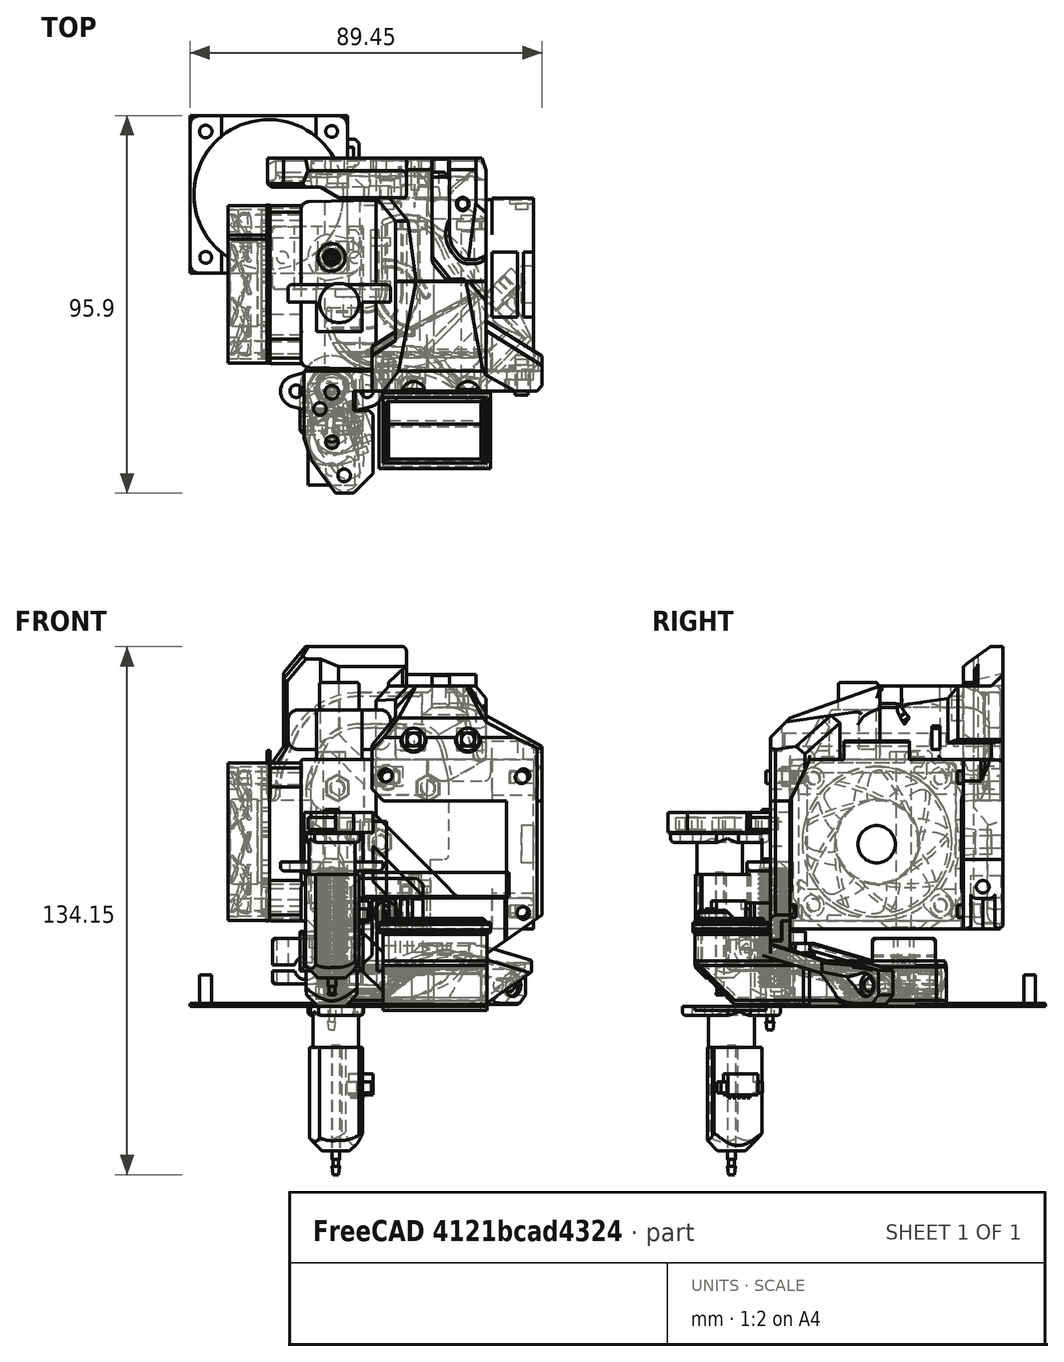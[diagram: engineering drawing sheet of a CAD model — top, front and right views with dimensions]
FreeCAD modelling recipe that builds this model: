
FCSTD DOCUMENT  (FreeCAD 0.18R16146 (Git))
Label: bearmera-4020-rev-1
License: All rights reserved
LicenseURL: http://en.wikipedia.org/wiki/All_rights_reserved
objects: Part::Box×71, Part::Cut×55, Part::Feature×46, Part::MultiFuse×39, Part::Chamfer×34, Part::Cylinder×33, Sketcher::SketchObject×6, PartDesign::Body×4, App::DocumentObjectGroup×3, Part::MultiCommon×3, Mesh::Feature×2, PartDesign::AdditiveLoft×2, PartDesign::Pad×2, App::Part×1
note: 299 computed .brp shape members not serialized (recipe doc carries the construction recipe); baked Part::Feature solids carry a one-line shape summary decoded from their .brp

FEATURE [Part::Feature] Part__Feature018  label="NOZZLE-POS"
  Placement = pos=(-0.025,3.1e-14,12.45) rot=(0.707107,0.707107,0;3.14159rad)
  shape: bbox 8.083 x 7 x 12.5 mm, 18 faces (baked)
FEATURE [Part::Feature] Part__Feature017  label="v6_heaterblock v1"
  Placement = pos=(-14.9885,-8.00025,5.758) rot=(0,0,1;0rad)
  shape: bbox 23 x 16 x 11.5 mm, 37 faces (baked)
FEATURE [Part::Feature] Part__Feature013  label="stepper"
  Placement = pos=(51.225,-28.9,19.7) rot=(0,0,1;1.5708rad)
  shape: bbox 40 x 44 x 47.7 mm, 101 faces (baked)
FEATURE [Part::Feature] Part__Feature014  label="heatsink"
  Placement = pos=(11.225,-28.4,19.7) rot=(0,0,1;1.5708rad)
  shape: bbox 30.92 x 43.26 x 62.61 mm, 110 faces (baked)
FEATURE [Part::Feature] Part__Feature016  label="e3d_hemera_fan v1"
  Placement = pos=(-15.775,13.2,61.8) rot=(0.57735,-0.57735,0.57735;4.18879rad)
  shape: bbox 10.51 x 40.01 x 40.01 mm, 129 faces (baked)
FEATURE [Mesh::Feature] lower_4020_fan_duct  label="lower_4020-fan-duct"
  Placement = pos=(11.3,-33.9,19.8) rot=(0,0,1;0rad)
FEATURE [Part::Feature] Cut007002001001  label="fan-mount-frame001"
  shape: bbox 28.2 x 19.2 x 3.5 mm, 16 faces (baked)
FEATURE [Part::Feature] Part__Feature  label="duct001"
  Placement = pos=(13,-15,0) rot=(0,0,1;0rad)
  shape: bbox 62.87 x 53.67 x 16.75 mm, 145 faces (baked)
FEATURE [Part::Feature] Part__Feature025  label="duct002"
  Placement = pos=(13,-15,0) rot=(0,0,1;0rad)
  shape: bbox 62.87 x 53.67 x 16.75 mm, 145 faces (baked)
FEATURE [Part::Box] Box  label="Cube"
  AttacherType = Attacher::AttachEngine3D
  Height = 17
  Length = 29
  Placement = pos=(26,-38,0) rot=(0,0,1;0rad)
  Width = 48
FEATURE [Part::Box] Box001  label="Cube001"
  AttacherType = Attacher::AttachEngine3D
  Height = 27
  Length = 26
  Placement = pos=(0,-34,0) rot=(0,0,1;0rad)
  Width = 10
FEATURE [Part::Cut] Cut
  Base = -> Part__Feature
  Tool = -> Box
FEATURE [Part::Cut] Cut007002001002
  Base = -> Cut
  Placement = pos=(0,0,-0.45) rot=(0,0,1;0rad)
  Tool = -> Box001
FEATURE [Part::Box] Box002  label="Cube002"
  AttacherType = Attacher::AttachEngine3D
  Height = 2
  Length = 13
  Placement = pos=(13,-24,0.8) rot=(0,0,1;0rad)
  Width = 4
FEATURE [Part::Box] Box003  label="Cube003"
  AttacherType = Attacher::AttachEngine3D
  Height = 1
  Length = 5
  Placement = pos=(21,-24,0.8) rot=(0,0,1;0rad)
  Width = 13
FEATURE [Part::Cut] Cut007002001003
  Base = -> Cut007002001002
  Tool = -> Box002
FEATURE [Part::Cut] Cut007002001004
  Base = -> Cut007002001003
  Tool = -> Box003
FEATURE [Part::Box] Box004  label="Cube004"
  AttacherType = Attacher::AttachEngine3D
  Height = 10
  Length = 24
  Placement = pos=(7,-30,10) rot=(0,0,1;0rad)
  Width = 27
FEATURE [Part::Cut] Cut007002001005
  Base = -> Cut007002001004
  Tool = -> Box004
FEATURE [Part::Box] Box005  label="Cube005"
  AttacherType = Attacher::AttachEngine3D
  Height = 10
  Length = 32
  Placement = pos=(-2,-38,0) rot=(0,0,1;0rad)
  Width = 14
FEATURE [Part::Box] Box007  label="Cube007"
  AttacherType = Attacher::AttachEngine3D
  Height = 10
  Length = 21
  Placement = pos=(26,-24,0) rot=(0,0,1;0rad)
  Width = 21
FEATURE [Part::Box] Box008  label="Cube008"
  AttacherType = Attacher::AttachEngine3D
  Height = 1
  Length = 41
  Placement = pos=(10,-35,9) rot=(0,0,1;0.506145rad)
  Width = 10
FEATURE [Part::MultiFuse] Fusion
  Shapes = -> [Cut007002001005,Box008]
FEATURE [Part::Cut] Cut007002001006
  Base = -> Fusion
  Tool = -> Box005
FEATURE [Part::Cut] Cut007002001007  label="duct-square-cut"
  Base = -> Cut007002001006
  Tool = -> Box007
FEATURE [Part::Feature] Cut007002001007001  label="Cut007002001008"
  shape: bbox 41.3 x 51.61 x 10 mm, 88 faces (baked)
FEATURE [Part::Box] Box012  label="Cube012"
  AttacherType = Attacher::AttachEngine3D
  Height = 1
  Length = 26.5
  Placement = pos=(13,-53,0) rot=(0,0,1;0rad)
  Width = 18
FEATURE [Part::Box] Box013  label="Cube013"
  AttacherType = Attacher::AttachEngine3D
  Height = 1
  Length = 23.5
  Placement = pos=(14.5,-51.5,0) rot=(0,0,1;0rad)
  Width = 15
FEATURE [Part::Cut] Cut007002001007002
  Base = -> Box012
  Placement = pos=(0,0,-1) rot=(0,0,1;0rad)
  Tool = -> Box013
FEATURE [Sketcher::SketchObject] Sketch
  AttachmentOffset = pos=(0,0,19) rot=(0,0,1;0rad)
  MapMode = 5
  Placement = pos=(0,0,19) rot=(0,0,1;0rad)
  Support = -> [XY_Plane]
  sketch-geometry (8):
    g0: LineSegment StartX=13 StartY=-35 StartZ=0 EndX=39.5 EndY=-35 EndZ=0
    g1: LineSegment StartX=39.5 StartY=-35 StartZ=0 EndX=39.5 EndY=-53 EndZ=0
    g2: LineSegment StartX=39.5 StartY=-53 StartZ=0 EndX=13 EndY=-53 EndZ=0
    g3: LineSegment StartX=13 StartY=-53 StartZ=0 EndX=13 EndY=-35 EndZ=0
    g4: LineSegment StartX=14.5 StartY=-36.5 StartZ=0 EndX=38 EndY=-36.5 EndZ=0
    g5: LineSegment StartX=38 StartY=-36.5 StartZ=0 EndX=38 EndY=-51.5 EndZ=0
    g6: LineSegment StartX=38 StartY=-51.5 StartZ=0 EndX=14.5 EndY=-51.5 EndZ=0
    g7: LineSegment StartX=14.5 StartY=-51.5 StartZ=0 EndX=14.5 EndY=-36.5 EndZ=0
  constraints (16):
    c: Coincident(g0,g1)
    c: Coincident(g1,g2)
    c: Coincident(g2,g3)
    c: Coincident(g3,g0)
    c: Horizontal(g0)
    c: Horizontal(g2)
    c: Vertical(g1)
    c: Vertical(g3)
    c: Coincident(g4,g5)
    c: Coincident(g5,g6)
    c: Coincident(g6,g7)
    c: Coincident(g7,g4)
    c: Horizontal(g4)
    c: Horizontal(g6)
    c: Vertical(g5)
    c: Vertical(g7)
FEATURE [Sketcher::SketchObject] Sketch001
  AttachmentOffset = pos=(0,0,10.45) rot=(0,0,1;0rad)
  MapMode = 5
  Placement = pos=(0,0,10.45) rot=(0,0,1;0rad)
  Support = -> [XY_Plane]
  sketch-geometry (8):
    g0: LineSegment StartX=13 StartY=-53 StartZ=0 EndX=39.5 EndY=-53 EndZ=0
    g1: LineSegment StartX=39.5 StartY=-53 StartZ=0 EndX=39.5 EndY=-24 EndZ=0
    g2: LineSegment StartX=39.5 StartY=-24 StartZ=0 EndX=13 EndY=-24 EndZ=0
    g3: LineSegment StartX=13 StartY=-24 StartZ=0 EndX=13 EndY=-53 EndZ=0
    g4: LineSegment StartX=38 StartY=-25.5 StartZ=0 EndX=14.5 EndY=-25.5 EndZ=0
    g5: LineSegment StartX=14.5 StartY=-25.5 StartZ=0 EndX=14.5 EndY=-51.5 EndZ=0
    g6: LineSegment StartX=14.5 StartY=-51.5 StartZ=0 EndX=38 EndY=-51.5 EndZ=0
    g7: LineSegment StartX=38 StartY=-51.5 StartZ=0 EndX=38 EndY=-25.5 EndZ=0
  constraints (16):
    c: Coincident(g0,g1)
    c: Coincident(g1,g2)
    c: Coincident(g2,g3)
    c: Coincident(g3,g0)
    c: Horizontal(g0)
    c: Horizontal(g2)
    c: Vertical(g1)
    c: Vertical(g3)
    c: Coincident(g4,g5)
    c: Coincident(g5,g6)
    c: Coincident(g6,g7)
    c: Coincident(g7,g4)
    c: Horizontal(g4)
    c: Horizontal(g6)
    c: Vertical(g5)
    c: Vertical(g7)
FEATURE [PartDesign::AdditiveLoft] AdditiveLoft
  Closed = false
  Profile = -> Sketch
  Ruled = false
  Sections = -> [Sketch001]
FEATURE [PartDesign::Body] Body  label="ramp"
  Group = -> [Sketch,Sketch001,AdditiveLoft]
  Origin = -> Origin
  Tip = -> AdditiveLoft
FEATURE [Part::Feature] Body001  label="ramp001"
  Placement = pos=(0,0,-0.45) rot=(0,0,1;0rad)
  shape: bbox 26.5 x 29 x 8.55 mm, 10 faces (baked)
FEATURE [Sketcher::SketchObject] Sketch002  label="Sketch003"
  AttachmentOffset = pos=(0,0,0.45) rot=(0,0,1;0rad)
  MapMode = 5
  Placement = pos=(0,0,0.45) rot=(0,0,1;0rad)
  Support = -> [XY_Plane001]
  sketch-geometry (8):
    g0: LineSegment StartX=39.5 StartY=-24 StartZ=0 EndX=13 EndY=-24 EndZ=0
    g1: LineSegment StartX=13 StartY=-24 StartZ=0 EndX=13 EndY=-43 EndZ=0
    g2: LineSegment StartX=13 StartY=-43 StartZ=0 EndX=39.5 EndY=-43 EndZ=0
    g3: LineSegment StartX=39.5 StartY=-43 StartZ=0 EndX=39.5 EndY=-24 EndZ=0
    g4: LineSegment StartX=38 StartY=-25.5 StartZ=0 EndX=14.5 EndY=-25.5 EndZ=0
    g5: LineSegment StartX=14.5 StartY=-25.5 StartZ=0 EndX=14.5 EndY=-41.5 EndZ=0
    g6: LineSegment StartX=14.5 StartY=-41.5 StartZ=0 EndX=38 EndY=-41.5 EndZ=0
    g7: LineSegment StartX=38 StartY=-41.5 StartZ=0 EndX=38 EndY=-25.5 EndZ=0
  constraints (16):
    c: Coincident(g0,g1)
    c: Coincident(g1,g2)
    c: Coincident(g2,g3)
    c: Coincident(g3,g0)
    c: Horizontal(g0)
    c: Horizontal(g2)
    c: Vertical(g1)
    c: Vertical(g3)
    c: Coincident(g4,g5)
    c: Coincident(g5,g6)
    c: Coincident(g6,g7)
    c: Coincident(g7,g4)
    c: Horizontal(g4)
    c: Horizontal(g6)
    c: Vertical(g5)
    c: Vertical(g7)
FEATURE [Sketcher::SketchObject] Sketch003  label="Sketch004"
  AttachmentOffset = pos=(0,0,10.45) rot=(0,0,1;0rad)
  MapMode = 5
  Placement = pos=(0,0,10.45) rot=(0,0,1;0rad)
  Support = -> [XY_Plane001]
  sketch-geometry (8):
    g0: LineSegment StartX=13 StartY=-24 StartZ=0 EndX=39.5 EndY=-24 EndZ=0
    g1: LineSegment StartX=39.5 StartY=-24 StartZ=0 EndX=39.5 EndY=-53 EndZ=0
    g2: LineSegment StartX=39.5 StartY=-53 StartZ=0 EndX=13 EndY=-53 EndZ=0
    g3: LineSegment StartX=13 StartY=-53 StartZ=0 EndX=13 EndY=-24 EndZ=0
    g4: LineSegment StartX=14.5 StartY=-25.5 StartZ=0 EndX=38 EndY=-25.5 EndZ=0
    g5: LineSegment StartX=38 StartY=-25.5 StartZ=0 EndX=38 EndY=-51.5 EndZ=0
    g6: LineSegment StartX=38 StartY=-51.5 StartZ=0 EndX=14.5 EndY=-51.5 EndZ=0
    g7: LineSegment StartX=14.5 StartY=-51.5 StartZ=0 EndX=14.5 EndY=-25.5 EndZ=0
  constraints (16):
    c: Coincident(g0,g1)
    c: Coincident(g1,g2)
    c: Coincident(g2,g3)
    c: Coincident(g3,g0)
    c: Horizontal(g0)
    c: Horizontal(g2)
    c: Vertical(g1)
    c: Vertical(g3)
    c: Coincident(g4,g5)
    c: Coincident(g5,g6)
    c: Coincident(g6,g7)
    c: Coincident(g7,g4)
    c: Horizontal(g4)
    c: Horizontal(g6)
    c: Vertical(g5)
    c: Vertical(g7)
FEATURE [PartDesign::AdditiveLoft] AdditiveLoft001
  Closed = false
  Profile = -> Sketch003
  Ruled = false
  Sections = -> [Sketch002]
FEATURE [PartDesign::Body] Body002  label="lower-ramp"
  Group = -> [Sketch002,Sketch003,AdditiveLoft001]
  Origin = -> Origin001
  Tip = -> AdditiveLoft001
FEATURE [Part::Feature] Body002002  label="lower-ramp002"
  Placement = pos=(0,0,-0.45) rot=(0,0,1;0rad)
  shape: bbox 26.5 x 29 x 10 mm, 10 faces (baked)
FEATURE [Sketcher::SketchObject] Sketch004  label="Sketch005"
  MapMode = 5
  Support = -> [XY_Plane002]
  sketch-geometry (31):
    g0: GeomPoint X=26 Y=-24 Z=0
    g1: LineSegment StartX=26 StartY=-24 StartZ=0 EndX=1.71 EndY=-24 EndZ=0
    g2: LineSegment StartX=26 StartY=-24 StartZ=0 EndX=26 EndY=8.3 EndZ=0
    g3: LineSegment StartX=13 StartY=-31 StartZ=0 EndX=14.5 EndY=-31 EndZ=0
    g4: LineSegment StartX=14.5 StartY=-31 StartZ=0 EndX=14.5 EndY=-25.5 EndZ=0
    g5: LineSegment StartX=14.5 StartY=-25.5 StartZ=0 EndX=39.5 EndY=-25.5 EndZ=0
    g6: LineSegment StartX=39.5 StartY=-25.5 StartZ=0 EndX=39.5 EndY=-24 EndZ=0
    g7-g12: Circle [constr] x6 (B-spline internal-alignment scaffolding for g13; pole/knot coordinates omitted)
    g13: BSplineCurve PolesCount=6 KnotsCount=4 Degree=3 IsPeriodic=0
    g14-g17: GeomPoint [constr] x4 (B-spline internal-alignment scaffolding for g13; pole/knot coordinates omitted)
    g18-g24: Circle [constr] x7 (B-spline internal-alignment scaffolding for g25; pole/knot coordinates omitted)
    g25: BSplineCurve PolesCount=7 KnotsCount=5 Degree=3 IsPeriodic=0
    g26-g30: GeomPoint [constr] x5 (B-spline internal-alignment scaffolding for g25; pole/knot coordinates omitted)
  constraints (24):
    c: DistanceY(g0,g-1) = 24
    c: DistanceX(g-1,g0) = 26
    c: Coincident(g1,g0)
    c: Horizontal(g1)
    c: Coincident(g2,g0)
    c: Vertical(g2)
    c: Coincident(g3,g4)
    c: Vertical(g4)
    c: Coincident(g4,g5)
    c: Horizontal(g5)
    c: Coincident(g5,g6)
    c: DistanceY(g2,g2) = 32.3
    c: Coincident(g13,g1)
    c: Radius(g7) = 0.6
    c: Equal(g7, g8-g12) x5
    c: Coincident(g13,g3)
    c: InternalAlignment(g7-g12 -> g13) x6
    c: InternalAlignment(g14-g17 -> g13) x4
    c: Coincident(g25,g2)
    c: Radius(g18) = 1
    c: Equal(g18, g19-g24) x6
    c: Coincident(g25,g6)
    c: InternalAlignment(g18-g24 -> g25) x7
    c: InternalAlignment(g26-g30 -> g25) x5
FEATURE [PartDesign::Pad] Pad
  Length = 10
  Length2 = 100
  Profile = -> Sketch004
  Type = 0
FEATURE [PartDesign::Body] Body002003  label="outer"
  Group = -> [Sketch004,Pad]
  Origin = -> Origin002
  Tip = -> Pad
FEATURE [Sketcher::SketchObject] Sketch005  label="Sketch006"
  MapMode = 5
  Support = -> [XY_Plane003]
  sketch-geometry (29):
    g0: GeomPoint X=26 Y=-24 Z=0
    g1: LineSegment StartX=26 StartY=-24 StartZ=0 EndX=3.42 EndY=-24 EndZ=0
    g2: LineSegment StartX=26 StartY=-24 StartZ=0 EndX=26 EndY=6.6 EndZ=0
    g3: GeomPoint X=14.5 Y=-30 Z=0
    g4: GeomPoint X=38 Y=-25.5 Z=0
    g5-g10: Circle [constr] x6 (B-spline internal-alignment scaffolding for g11; pole/knot coordinates omitted)
    g11: BSplineCurve PolesCount=6 KnotsCount=4 Degree=3 IsPeriodic=0
    g12-g15: GeomPoint [constr] x4 (B-spline internal-alignment scaffolding for g11; pole/knot coordinates omitted)
    g16-g21: Circle [constr] x6 (B-spline internal-alignment scaffolding for g22; pole/knot coordinates omitted)
    g22: BSplineCurve PolesCount=6 KnotsCount=4 Degree=3 IsPeriodic=0
    g23-g26: GeomPoint [constr] x4 (B-spline internal-alignment scaffolding for g22; pole/knot coordinates omitted)
    g27: LineSegment StartX=14.5 StartY=-30 StartZ=0 EndX=14.5 EndY=-25.5 EndZ=0
    g28: LineSegment StartX=14.5 StartY=-25.5 StartZ=0 EndX=38 EndY=-25.5 EndZ=0
  constraints (29):
    c: DistanceY(g0,g-1) = 24
    c: DistanceX(g-1,g0) = 26
    c: Coincident(g1,g0)
    c: Horizontal(g1)
    c: Coincident(g2,g0)
    c: Vertical(g2)
    c: DistanceY(g2,g2) = 30.6
    c: DistanceX(g1,g1) = 22.58
    c: DistanceY(g4,g-1) = 25.5
    c: DistanceX(g-1,g4) = 38
    c: DistanceY(g3,g-1) = 30
    c: DistanceX(g-1,g3) = 14.5
    c: Coincident(g11,g1)
    c: Radius(g5) = 0.4
    c: Equal(g5, g6-g10) x5
    c: Coincident(g11,g3)
    c: InternalAlignment(g5-g10 -> g11) x6
    c: InternalAlignment(g12-g15 -> g11) x4
    c: Coincident(g22,g2)
    c: Radius(g16) = 1
    c: Equal(g16, g17-g21) x5
    c: Coincident(g22,g4)
    c: InternalAlignment(g16-g21 -> g22) x6
    c: InternalAlignment(g23-g26 -> g22) x4
    c: Coincident(g27,g3)
    c: Vertical(g27)
    c: Coincident(g28,g27)
    c: Coincident(g28,g4)
    c: Horizontal(g28)
FEATURE [PartDesign::Pad] Pad001
  Length = 8.2
  Length2 = 100
  Profile = -> Sketch005
  Type = 0
FEATURE [PartDesign::Body] Body002004  label="inner"
  Group = -> [Sketch005,Pad001]
  Origin = -> Origin003
  Tip = -> Pad001
FEATURE [App::DocumentObjectGroup] Group001  label="Sketch002"
  Group = -> [Body,Body002,Body002003,Body002004]
FEATURE [Part::Feature] Body002004001  label="inner001"
  Placement = pos=(0,0,0.8) rot=(0,0,1;0rad)
  shape: bbox 34.69 x 36.6 x 8.2 mm, 8 faces (baked)
FEATURE [Part::Box] Box015  label="Cube015"
  AttacherType = Attacher::AttachEngine3D
  Height = 8.2
  Length = 23.5
  Placement = pos=(14.5,-27,0.8) rot=(0,0,1;0rad)
  Width = 5
FEATURE [Part::Box] Box016  label="Cube016"
  AttacherType = Attacher::AttachEngine3D
  Height = 0.8
  Length = 23.5
  Placement = pos=(14.5,-42.5,0) rot=(0,0,1;0rad)
  Width = 18
FEATURE [Part::Feature] Body002003001  label="outer001"
  shape: bbox 37.79 x 39.3 x 10 mm, 10 faces (baked)
FEATURE [Part::Feature] Body002004002  label="inner002"
  Placement = pos=(0,0,0.8) rot=(0,0,1;0rad)
  shape: bbox 34.69 x 36.6 x 8.2 mm, 8 faces (baked)
FEATURE [Part::Feature] Cut007002001007009  label="fan-mount-frame002"
  Placement = pos=(0,0,-0.45) rot=(0,0,1;0rad)
  shape: bbox 28.2 x 19.2 x 3.5 mm, 16 faces (baked)
FEATURE [Part::Cut] Cut007002001007010
  Base = -> Body002003001
  Tool = -> Body002004001
FEATURE [Part::MultiFuse] Fusion001
  Shapes = -> [Box016,Body002002]
FEATURE [Part::Cut] Cut007002001007011
  Base = -> Fusion001
  Tool = -> Box015
FEATURE [Part::Cut] Cut007002001007012
  Base = -> Cut007002001007011
  Tool = -> Body002004002
FEATURE [Part::MultiFuse] Fusion002
  Shapes = -> [Body001,Cut007002001007012]
FEATURE [Part::MultiFuse] Fusion003
  Shapes = -> [Fusion002,Cut007002001007010]
FEATURE [Part::MultiFuse] Fusion004
  Placement = pos=(0,0,1) rot=(0,0,1;0rad)
  Shapes = -> [Fusion003,Cut007002001007001]
FEATURE [Part::Box] Box017  label="Cube017"
  AttacherType = Attacher::AttachEngine3D
  Height = 0.8
  Length = 4
  Placement = pos=(10,-25,1.8) rot=(0,0,1;0rad)
  Width = 4
FEATURE [Part::Box] Box018  label="Cube018"
  AttacherType = Attacher::AttachEngine3D
  Height = 1
  Length = 36.5
  Placement = pos=(5.64694,-26.4947,8.5) rot=(0,0,1;0.488692rad)
  Width = 1
FEATURE [Part::Box] Box019  label="Cube019"
  AttacherType = Attacher::AttachEngine3D
  Height = 1
  Length = 35.5
  Placement = pos=(3.75,-25.25,9.1) rot=(0,0,1;0rad)
  Width = 1
FEATURE [Part::Chamfer] Chamfer005
  Base = -> Box018
  Edges = 1 edges r=0.5: [Edge9]
  Placement = pos=(0,0,1) rot=(0,0,1;0rad)
FEATURE [Part::Cylinder] Cylinder001  label="stepper-screw-pos"
  Angle = 360
  AttacherType = Attacher::AttachEngine3D
  Height = 10
  Placement = pos=(48.73,-25,58.7) rot=(1,0,0;1.5708rad)
  Radius = 1.65
FEATURE [Part::Cylinder] Cylinder002  label="fill"
  Angle = 360
  AttacherType = Attacher::AttachEngine3D
  Height = 5
  Placement = pos=(48.23,-28.9,58.2) rot=(1,0,0;1.5708rad)
  Radius = 3
FEATURE [Part::Cylinder] Cylinder003  label="fill001"
  Angle = 360
  AttacherType = Attacher::AttachEngine3D
  Height = 5
  Placement = pos=(14.23,-28.9,58.2) rot=(1,0,0;1.5708rad)
  Radius = 3
FEATURE [Part::Box] Box020  label="Cube020"
  AttacherType = Attacher::AttachEngine3D
  Height = 4
  Length = 4
  Placement = pos=(10,-28.9,56) rot=(0,0,1;0rad)
  Width = 3
FEATURE [Part::Box] Box021  label="Cube021"
  AttacherType = Attacher::AttachEngine3D
  Height = 6
  Length = 4
  Placement = pos=(48.55,-28.9,55.2) rot=(0,0,1;0rad)
  Width = 5
FEATURE [Part::Cylinder] Cylinder004  label="stepper-screw-pos001"
  Angle = 360
  AttacherType = Attacher::AttachEngine3D
  Height = 10
  Placement = pos=(13.73,-25,58.7) rot=(1,0,0;1.5708rad)
  Radius = 1.65
FEATURE [Part::Cylinder] Cylinder005  label="stepper-screw-pos002"
  Angle = 360
  AttacherType = Attacher::AttachEngine3D
  Height = 10
  Placement = pos=(48.23,-25,58.2) rot=(1,0,0;1.5708rad)
  Radius = 1.6
FEATURE [Part::Cylinder] Cylinder006  label="stepper-screw-pos003"
  Angle = 360
  AttacherType = Attacher::AttachEngine3D
  Height = 10
  Placement = pos=(13.73,-25,25.1) rot=(1,0,0;1.5708rad)
  Radius = 0.5
FEATURE [Part::Cylinder] Cylinder007  label="stepper-screw-pos004"
  Angle = 360
  AttacherType = Attacher::AttachEngine3D
  Height = 10
  Placement = pos=(48.73,-25,23.7) rot=(1,0,0;1.5708rad)
  Radius = 1.6
FEATURE [Part::Feature] Part__Feature012001  label="body_front001"
  Placement = pos=(-5.275,25.1,21) rot=(0,0,-1;1.5708rad)
  shape: bbox 44.13 x 28.92 x 79.97 mm, 174 faces (baked)
FEATURE [Part::Feature] Part__Feature012002  label="body_front002"
  Placement = pos=(-5.275,25.1,21) rot=(0,0,-1;1.5708rad)
  shape: bbox 44.13 x 28.92 x 79.97 mm, 174 faces (baked)
FEATURE [Part::MultiFuse] Fusion008
  Shapes = -> [Part__Feature012002,Cylinder003]
FEATURE [Part::MultiFuse] Fusion009
  Shapes = -> [Fusion008,Cylinder002]
FEATURE [Part::Cut] Cut007002001007014
  Base = -> Fusion009
  Tool = -> Box020
FEATURE [Part::Cut] Cut007002001007015
  Base = -> Cut007002001007014
  Tool = -> Box021
FEATURE [Part::Cut] Cut007002001007016
  Base = -> Cut007002001007015
  Tool = -> Cylinder001
FEATURE [Part::Cut] Cut007002001007017
  Base = -> Cut007002001007016
  Tool = -> Cylinder004
FEATURE [Part::Box] Box022  label="Cube022"
  AttacherType = Attacher::AttachEngine3D
  Height = 5
  Length = 7
  Placement = pos=(11,-31,56) rot=(0,0,1;0rad)
  Width = 10
FEATURE [Part::MultiCommon] Common  label="body-pos-fix"
  Shapes = -> [Box022,Part__Feature012001]
FEATURE [Part::Feature] Common001  label="body-pos-fix001"
  Placement = pos=(0,0,-34) rot=(0,0,1;0rad)
  shape: bbox 7 x 3.1 x 5 mm, 23 faces (baked)
FEATURE [Part::Box] Box023  label="Cube023"
  AttacherType = Attacher::AttachEngine3D
  Height = 10
  Length = 10
  Placement = pos=(4,-28.9,19) rot=(0,0,1;0rad)
  Width = 10
FEATURE [Part::Cut] Cut007002001007018
  Base = -> Common001
  Tool = -> Box023
FEATURE [Part::Cylinder] Cylinder008  label="tmpp"
  Angle = 360
  AttacherType = Attacher::AttachEngine3D
  Height = 2.1
  Placement = pos=(14.23,-28.9,24.2) rot=(1,0,0;1.5708rad)
  Radius = 1.7
FEATURE [Part::MultiFuse] Fusion010  label="body-pos-2"
  Shapes = -> [Cylinder008,Cut007002001007018]
FEATURE [Part::Box] Box024  label="Cube024"
  AttacherType = Attacher::AttachEngine3D
  Height = 14
  Length = 41
  Placement = pos=(10.23,-33.9,13.5) rot=(0,0,1;0rad)
  Width = 5
FEATURE [Part::Cylinder] Cylinder009  label="stepper-screw-pos005"
  Angle = 360
  AttacherType = Attacher::AttachEngine3D
  Height = 12
  Placement = pos=(13.73,-31,26.4) rot=(1,0,0;1.5708rad)
  Radius = 0.5
FEATURE [Part::Feature] Fusion010002  label="body-pos-1"
  Placement = pos=(62.4,0,48.4) rot=(0,1,0;3.14159rad)
  shape: bbox 7 x 3.1 x 5 mm, 25 faces (baked)
FEATURE [Part::Box] Box026  label="Cube026"
  AttacherType = Attacher::AttachEngine3D
  Height = 10
  Length = 30
  Placement = pos=(40.8236,-35.5,2.21194) rot=(0,-1,0;0.610865rad)
  Width = 10
FEATURE [Part::Box] Box027  label="Cube027"
  AttacherType = Attacher::AttachEngine3D
  Height = 10
  Length = 10
  Placement = pos=(51.23,-38,19) rot=(0,0,1;0rad)
  Width = 10
FEATURE [Part::Box] Box028  label="Cube028"
  AttacherType = Attacher::AttachEngine3D
  Height = 29
  Length = 10
  Placement = pos=(44,-41,0) rot=(0,0,1;0rad)
  Width = 10
FEATURE [Part::Cylinder] Cylinder010  label="stepper-screw-pos006"
  Angle = 360
  AttacherType = Attacher::AttachEngine3D
  Height = 10
  Placement = pos=(48.73,-25,25.1) rot=(1,0,0;1.5708rad)
  Radius = 0.5
FEATURE [Part::Cylinder] Cylinder011  label="stepper-screw-pos007"
  Angle = 360
  AttacherType = Attacher::AttachEngine3D
  Height = 10
  Placement = pos=(48.73,-25,23.7) rot=(1,0,0;1.5708rad)
  Radius = 1.6
FEATURE [Part::Cylinder] Cylinder012  label="stepper-screw-pos008"
  Angle = 360
  AttacherType = Attacher::AttachEngine3D
  Height = 12
  Placement = pos=(13.73,-31,23.7) rot=(1,0,0;1.5708rad)
  Radius = 3
FEATURE [Part::Cylinder] Cylinder013  label="stepper-screw-pos009"
  Angle = 360
  AttacherType = Attacher::AttachEngine3D
  Height = 10
  Placement = pos=(13.73,-25,23.7) rot=(1,0,0;1.5708rad)
  Radius = 1.6
FEATURE [Part::Cylinder] Cylinder014  label="stepper-screw-pos010"
  Angle = 360
  AttacherType = Attacher::AttachEngine3D
  Height = 12
  Placement = pos=(13.73,-31.2,23.7) rot=(1,0,0;1.5708rad)
  Radius = 3
FEATURE [Part::Box] Box029  label="Cube029"
  AttacherType = Attacher::AttachEngine3D
  Height = 10
  Length = 10
  Placement = pos=(9,-29,13.8) rot=(0,0,1;0rad)
  Width = 10
FEATURE [Part::Chamfer] Chamfer009
  Base = -> Box029
  Edges = 1 edges r=2: [Edge10]
  Placement = pos=(0,0.1,1) rot=(0,0,1;0rad)
FEATURE [Part::Feature] Chamfer009001  label="Chamfer010"
  Placement = pos=(32,0.1,1) rot=(0,0,1;0rad)
  shape: bbox 10 x 10 x 10 mm, 7 faces (baked)
FEATURE [Part::Box] Box030  label="Cube030"
  AttacherType = Attacher::AttachEngine3D
  Height = 60
  Length = 63
  Placement = pos=(0,-43.2,-7.8) rot=(0,0,1;0rad)
  Width = 30
FEATURE [Part::Cut] Cut007002001007029003002  label="tmp-body-front"
  Base = -> Cut007002001007017
  Tool = -> Box030
FEATURE [Part::Feature] Part__Feature011  label="body_back"
  Placement = pos=(-5.275,25.2,21) rot=(0,0,-1;1.5708rad)
  shape: bbox 55.53 x 31.22 x 71.72 mm, 411 faces (baked)
FEATURE [Part::Feature] Part__Feature020  label="pinda v4_y33"
  Placement = pos=(0.025,-33,5) rot=(0,0,-1;1.5708rad)
  shape: bbox 9.315 x 9.314 x 49.01 mm, 71 faces (baked)
FEATURE [Part::Feature] Box025001  label="Cube031"
  Placement = pos=(0,0,1.5) rot=(0,0,1;0rad)
  shape: bbox 23.5 x 14.03 x 14.03 mm, 6 faces (baked)
FEATURE [Part::MultiFuse] Fusion010008
  Shapes = -> [Cylinder007,Cylinder010]
FEATURE [Part::MultiFuse] Fusion010009
  Shapes = -> [Cylinder013,Cylinder006]
FEATURE [Part::MultiFuse] Fusion010010
  Shapes = -> [Cylinder012,Cylinder009]
FEATURE [Part::Cut] Cut007002001007029003011
  Base = -> Fusion004
  Tool = -> Box017
FEATURE [Part::Chamfer] Chamfer
  Base = -> Box019
  Edges = 1 edges r=0.5: [Edge9]
FEATURE [Part::Cut] Cut007002001007029003013
  Base = -> Box024
  Tool = -> Box025001
FEATURE [Part::Cut] Cut007002001007029003014
  Base = -> Fusion010
  Tool = -> Chamfer009
FEATURE [Part::Cut] Cut007002001007029003015
  Base = -> Fusion010002
  Tool = -> Chamfer009001
FEATURE [Part::MultiFuse] Fusion010014
  Shapes = -> [Cut007002001007029003013,Cut007002001007029003015]
FEATURE [Part::MultiFuse] Fusion010015
  Shapes = -> [Fusion010014,Cut007002001007029003014]
FEATURE [Part::Cut] Cut007002001007029003016
  Base = -> Fusion010015
  Tool = -> Box027
FEATURE [Part::Cut] Cut007002001007029003017
  Base = -> Cut007002001007029003016
  Tool = -> Box028
FEATURE [Part::Cut] Cut007002001007029003018
  Base = -> Cut007002001007029003017
  Tool = -> Fusion010008
FEATURE [Part::Cut] Cut007002001007029003019
  Base = -> Cut007002001007029003018
  Tool = -> Fusion010009
FEATURE [Part::Cut] Cut007002001007029003020
  Base = -> Cut007002001007029003019
  Tool = -> Fusion010010
FEATURE [Part::Cut] Cut007002001007029003021
  Base = -> Cut007002001007029003020
  Tool = -> Box026
FEATURE [Part::MultiFuse] Fusion010016
  Shapes = -> [Cut007002001007029003011,Chamfer]
FEATURE [Part::MultiFuse] Fusion010017
  Placement = pos=(0,0,0.5) rot=(0,0,1;0rad)
  Shapes = -> [Fusion010016,Chamfer005]
FEATURE [Part::Chamfer] Chamfer009002
  Base = -> Cut007002001007009
  Edges = 1 edges r=0.8: [Edge12]
FEATURE [Part::Chamfer] Chamfer009003
  Base = -> Chamfer009002
  Edges = 1 edges r=0.6: [Edge1]
FEATURE [Part::Chamfer] Chamfer009004
  Base = -> Chamfer009003
  Edges = 1 edges r=0.9: [Edge15]
FEATURE [Part::Box] Box025002  label="Cube032"
  AttacherType = Attacher::AttachEngine3D
  Height = 3
  Length = 1
  Placement = pos=(13,-52.2,20.85) rot=(0,0,1;0rad)
  Width = 9
FEATURE [Part::Chamfer] Chamfer009006
  Base = -> Cut007002001007029003021
  Edges = 1 edges r=3: [Edge4]
FEATURE [Part::Chamfer] Chamfer009007
  Base = -> Chamfer009006
  Edges = 2 edges r=1: [Edge3,Edge20]
FEATURE [Part::Feature] Fusion010020001  label="hemera-4020-duct-rev-1-refined"
  shape: bbox 52.67 x 64.46 x 26 mm, 194 faces (baked)
FEATURE [Part::Cylinder] Cylinder
  Angle = 360
  AttacherType = Attacher::AttachEngine3D
  Height = 10
  Radius = 1.6
FEATURE [Part::Cylinder] Cylinder015
  Angle = 360
  AttacherType = Attacher::AttachEngine3D
  Height = 8
  Placement = pos=(0,32,0) rot=(0,0,1;0rad)
  Radius = 1.5
FEATURE [Part::Cylinder] Cylinder016
  Angle = 360
  AttacherType = Attacher::AttachEngine3D
  Height = 8
  Placement = pos=(-32,0,0) rot=(0,0,1;0rad)
  Radius = 1.5
FEATURE [Part::Cylinder] Cylinder017
  Angle = 360
  AttacherType = Attacher::AttachEngine3D
  Height = 10
  Placement = pos=(-32,32,0) rot=(0,0,1;0rad)
  Radius = 1.6
FEATURE [Part::Cylinder] Cylinder018
  Angle = 360
  AttacherType = Attacher::AttachEngine3D
  Height = 10
  Placement = pos=(-16,16,0) rot=(0,0,1;0rad)
  Radius = 19
FEATURE [Part::Box] Box025003  label="Cube033"
  AttacherType = Attacher::AttachEngine3D
  Height = 0.7
  Length = 40
  Placement = pos=(-36,-4,0) rot=(0,0,1;0rad)
  Width = 40
FEATURE [Part::Cut] Cut007002001007029003024
  Base = -> Box025003
  Tool = -> Cylinder017
FEATURE [Part::Cut] Cut007002001007029003025
  Base = -> Cut007002001007029003024
  Tool = -> Cylinder
FEATURE [Part::Cut] Cut007002001007029003026
  Base = -> Cut007002001007029003025
  Tool = -> Cylinder018
FEATURE [Part::Feature] Fillet001
  shape: bbox 40 x 40 x 0.7 mm, 13 faces (baked)
FEATURE [Part::Feature] Fillet002
  shape: bbox 40 x 40 x 0.7 mm, 13 faces (baked)
FEATURE [Part::Box] Box025004  label="Cube034"
  AttacherType = Attacher::AttachEngine3D
  Height = 10
  Length = 8
  Placement = pos=(-4,-4,0) rot=(0,0,1;0rad)
  Width = 40
FEATURE [Part::Box] Box025005  label="Cube035"
  AttacherType = Attacher::AttachEngine3D
  Height = 10
  Length = 8
  Placement = pos=(-36,-4,0) rot=(0,0,1;0rad)
  Width = 40
FEATURE [Part::MultiCommon] Common002  label="fan-spacer-lower-tmp"
  Shapes = -> [Box025005,Fillet001]
FEATURE [Part::MultiCommon] Common003
  Shapes = -> [Fillet002,Box025004]
FEATURE [Part::Box] Box025006  label="Cube036"
  AttacherType = Attacher::AttachEngine3D
  Height = 0.7
  Length = 3
  Placement = pos=(4,0,0) rot=(0,0,1;0rad)
  Width = 7
FEATURE [Part::Box] Box025007  label="Cube037"
  AttacherType = Attacher::AttachEngine3D
  Height = 0.7
  Length = 1.5
  Placement = pos=(4,2,0) rot=(0,0,1;0rad)
  Width = 3
FEATURE [Part::MultiFuse] Fusion010020005  label="fan-spacer-lower"
  Shapes = -> [Common002,Cylinder016]
FEATURE [Part::Cut] Cut007002001007029003027
  Base = -> Box025006
  Tool = -> Box025007
FEATURE [Part::Chamfer] Chamfer009008
  Base = -> Cut007002001007029003027
  Edges = 2 edges r=1: [Edge20,Edge24]
FEATURE [Part::Feature] Chamfer009008001  label="Chamfer009009"
  Placement = pos=(0,23,0) rot=(0,0,1;0rad)
  shape: bbox 3 x 7 x 0.7 mm, 12 faces (baked)
FEATURE [Part::MultiFuse] Fusion010020006  label="fan-spacer-upper"
  Shapes = -> [Common003,Chamfer009008,Chamfer009008001,Cylinder015]
FEATURE [App::DocumentObjectGroup] Group002  label="export"
  Group = -> [Fusion010020006,Fusion010020005]
FEATURE [Mesh::Feature] turbo_fan_35x18_2_  label="4020-fan"
  Placement = pos=(31.25,-53.5,41.25) rot=(1,0,0;1.5708rad)
FEATURE [Part::Box] Box025009  label="Cube039"
  AttacherType = Attacher::AttachEngine3D
  Height = 1
  Length = 36
  Placement = pos=(10.5,-35.6,20.85) rot=(0,0,1;0rad)
  Width = 1.3
FEATURE [Part::Box] Box025010  label="Cube040"
  AttacherType = Attacher::AttachEngine3D
  Height = 1
  Length = 2
  Placement = pos=(11,-56.6,20.85) rot=(0,0,1;0rad)
  Width = 21.3
FEATURE [Part::Box] Box025011  label="Cube041"
  AttacherType = Attacher::AttachEngine3D
  Height = 1
  Length = 2
  Placement = pos=(39.5,-56.6,20.85) rot=(0,0,1;0rad)
  Width = 21.3
FEATURE [Part::Box] Box025012  label="Cube042"
  AttacherType = Attacher::AttachEngine3D
  Height = 1
  Length = 36
  Placement = pos=(10.5,-54.5,20.85) rot=(0,0,1;0rad)
  Width = 2.3
FEATURE [Part::Cut] Cut007002001007029003028
  Base = -> Fusion010020001
  Tool = -> Box025009
FEATURE [Part::Cut] Cut007002001007029003029
  Base = -> Cut007002001007029003028
  Tool = -> Box025010
FEATURE [Part::Cut] Cut007002001007029003030
  Base = -> Cut007002001007029003029
  Tool = -> Box025011
FEATURE [Part::Cut] Cut007002001007029003031
  Base = -> Cut007002001007029003030
  Tool = -> Box025012
FEATURE [Part::Feature] Cut007002001002005001  label="fan-mount-frame-lower"
  Placement = pos=(11.7,-54,18.85) rot=(0,0,1;0rad)
  shape: bbox 28.2 x 19.2 x 3.5 mm, 16 faces (baked)
FEATURE [Part::Feature] Cut007002001007029003032  label="fan-mount-frame-lower001"
  Placement = pos=(11.7,-54,18.85) rot=(0,0,1;0rad)
  shape: bbox 28.2 x 19.2 x 3.5 mm, 16 faces (baked)
FEATURE [Part::Chamfer] Chamfer009008005
  Base = -> Fusion010017
  Edges = 2 edges r=1: [Edge5,Edge7]
FEATURE [Part::Chamfer] Chamfer009008006
  Base = -> Box025002
  Edges = 1 edges r=1.5: [Edge12]
FEATURE [Part::MultiFuse] Fusion010020007
  Shapes = -> [Cut007002001007029003032,Chamfer009008006]
FEATURE [Part::Chamfer] Chamfer009008007
  Base = -> Fusion010020007
  Edges = 1 edges r=0.9: [Edge4]
FEATURE [Part::Chamfer] Chamfer009008008
  Base = -> Chamfer009008007
  Edges = 1 edges r=0.6: [Edge5]
FEATURE [Part::Chamfer] Chamfer009008009
  Base = -> Chamfer009008008
  Edges = 1 edges r=0.8: [Edge15]
FEATURE [Part::Cut] Cut007002001007029003033
  Base = -> Chamfer009008009
  Tool = -> Cylinder014
FEATURE [Part::MultiFuse] Fusion010020008
  Shapes = -> [Cut007002001007029003033,Chamfer009008005]
FEATURE [Part::MultiFuse] Fusion010020009  label="duct-rev-2"
  Shapes = -> [Fusion010020008,Chamfer009007]
FEATURE [Part::Feature] Fusion010020005001  label="fan-spacer-lower001"
  Placement = pos=(-16,-22.75,57.75) rot=(0,-1,0;1.5708rad)
  shape: bbox 8 x 40 x 8 mm, 13 faces (baked)
FEATURE [Part::Feature] Fusion010020006001  label="fan-spacer-upper001"
  Placement = pos=(-15.7,-22.75,58) rot=(0,-1,0;1.5708rad)
  shape: bbox 8 x 40 x 11 mm, 33 faces (baked)
FEATURE [Part::Box] Box025013  label="Cube043"
  AttacherType = Attacher::AttachEngine3D
  Height = 36
  Length = 9
  Placement = pos=(44.45,-33.9,16.64) rot=(0,0,1;0rad)
  Width = 5
FEATURE [Part::Chamfer] Chamfer009008010
  Base = -> Box025013
  Edges = 1 edges r=1.3: [Edge5]
FEATURE [Part::Cut] Cut007002001007029003034
  Base = -> Chamfer009008010
  Tool = -> Cylinder011
FEATURE [Part::Feature] Box025014001  label="Cube045"
  Placement = pos=(-6.4,0,14.95) rot=(0,0,1;0rad)
  shape: bbox 24.82 x 24 x 25.31 mm, 6 faces (baked)
FEATURE [Part::Cut] Cut007002001007029003035
  Base = -> Cut007002001007029003034
  Tool = -> Box025014001
FEATURE [Part::Box] Box025014002  label="Cube046"
  AttacherType = Attacher::AttachEngine3D
  Height = 12
  Length = 8
  Placement = pos=(43.3,-31.1,15.6) rot=(0,0,1;0rad)
  Width = 3
FEATURE [Part::Cut] Cut007002001007029003036
  Base = -> Cut007002001007029003035
  Tool = -> Box025014002
FEATURE [Part::MultiFuse] Fusion010020009002  label="front-rev-1"
  Shapes = -> [Cut007002001007029003002,Cut007002001007029003036]
FEATURE [Part::Cylinder] Cylinder019
  Angle = 360
  AttacherType = Attacher::AttachEngine3D
  Height = 10
  Placement = pos=(0,-33,10) rot=(0,0,1;0rad)
  Radius = 8
FEATURE [Part::Cylinder] Cylinder020
  Angle = 360
  AttacherType = Attacher::AttachEngine3D
  Height = 10
  Placement = pos=(0,-33,9) rot=(0,0,1;0rad)
  Radius = 4
FEATURE [Part::Box] Box025014003  label="Cube047"
  AttacherType = Attacher::AttachEngine3D
  Height = 10
  Length = 16
  Placement = pos=(-8,-45,10) rot=(0,0,1;0rad)
  Width = 12
FEATURE [Part::Box] Box025014004  label="Cube048"
  AttacherType = Attacher::AttachEngine3D
  Height = 11
  Length = 1.5
  Placement = pos=(-1,-46,9) rot=(0,0,1;0rad)
  Width = 12
FEATURE [Part::MultiFuse] Fusion010020009003
  Placement = pos=(0,0,-1) rot=(0,0,1;0rad)
  Shapes = -> [Box025014003,Cylinder019]
FEATURE [Part::Box] Box025014006  label="Cube050"
  AttacherType = Attacher::AttachEngine3D
  Height = 37
  Length = 4
  Placement = pos=(4,-33.9,10) rot=(0,0,1;0rad)
  Width = 5
FEATURE [Part::Box] Box025014007  label="Cube051"
  AttacherType = Attacher::AttachEngine3D
  Height = 19
  Length = 6
  Placement = pos=(8,-33.9,28) rot=(0,0,1;0rad)
  Width = 5
FEATURE [Part::Box] Box025014009  label="Cube053"
  AttacherType = Attacher::AttachEngine3D
  Height = 6
  Length = 37
  Placement = pos=(8,-33.9,28) rot=(0,0,1;0rad)
  Width = 5
FEATURE [Part::Cylinder] Cylinder021
  Angle = 360
  AttacherType = Attacher::AttachEngine3D
  Height = 20
  Placement = pos=(11,-40,15) rot=(0,-1,0;1.5708rad)
  Radius = 1.6
FEATURE [Part::Cylinder] Cylinder022
  Angle = 360
  AttacherType = Attacher::AttachEngine3D
  Height = 3
  Placement = pos=(-5,-40,17.8) rot=(0,-1,0;1.5708rad)
  Radius = 0.5
FEATURE [Part::Cylinder] Cylinder023
  Angle = 360
  AttacherType = Attacher::AttachEngine3D
  Height = 20
  Placement = pos=(11,-40,16.4) rot=(0,-1,0;1.5708rad)
  Radius = 0.5
FEATURE [Part::Cylinder] Cylinder024
  Angle = 360
  AttacherType = Attacher::AttachEngine3D
  Height = 3
  Placement = pos=(-5,-40,15) rot=(0,-1,0;1.5708rad)
  Radius = 3
FEATURE [Part::Box] Box025014010  label="Cube054"
  AttacherType = Attacher::AttachEngine3D
  Height = 6
  Length = 2
  Placement = pos=(3,-46,11) rot=(0,0,1;0rad)
  Width = 9
FEATURE [Part::MultiFuse] Fusion010020009004
  Placement = pos=(0,0,-1) rot=(0,0,1;0rad)
  Shapes = -> [Cylinder024,Cylinder022]
FEATURE [Part::MultiFuse] Fusion010020009005
  Placement = pos=(0,0,-1) rot=(0,0,1;0rad)
  Shapes = -> [Cylinder021,Cylinder023]
FEATURE [Part::Box] Box025014011  label="probe-mount-pos-arm"
  AttacherType = Attacher::AttachEngine3D
  Height = 6
  Length = 6
  Placement = pos=(5.23,-32.4,15) rot=(0,0,1;0rad)
  Width = 2
FEATURE [Part::Box] Box025014012  label="probe-mount-pos-arm001"
  AttacherType = Attacher::AttachEngine3D
  Height = 10
  Length = 6
  Placement = pos=(5.23,-32.5,10) rot=(0,0,1;0rad)
  Width = 2.2
FEATURE [Part::Chamfer] Chamfer009008015
  Base = -> Box025014012
  Edges = 1 edges r=2: [Edge6]
  Placement = pos=(0,0,2.3) rot=(0,0,1;0rad)
FEATURE [Part::Box] Box025014013  label="Cube055"
  AttacherType = Attacher::AttachEngine3D
  Height = 19
  Length = 5
  Placement = pos=(5.23,-33.9,9) rot=(0,0,1;0rad)
  Width = 5
FEATURE [Part::Cut] Cut007002001007029003042
  Base = -> Fusion010020009
  Tool = -> Chamfer009008015
FEATURE [Part::Chamfer] Chamfer009008018
  Base = -> Box025014011
  Edges = 2 edges r=1: [Edge6,Edge8]
FEATURE [Part::Box] Box025014014  label="Cube056"
  AttacherType = Attacher::AttachEngine3D
  Height = 5
  Length = 18
  Placement = pos=(5.23,-33.9,27.5) rot=(0,0,1;0rad)
  Width = 5
FEATURE [Part::Cylinder] Cylinder025
  Angle = 360
  AttacherType = Attacher::AttachEngine3D
  Height = 14
  Placement = pos=(19,-31.4,21) rot=(0,0,1;0rad)
  Radius = 0.9
FEATURE [Part::Cylinder] Cylinder026
  Angle = 360
  AttacherType = Attacher::AttachEngine3D
  Height = 14
  Placement = pos=(19,-31.4,25) rot=(0,0,1;0rad)
  Radius = 1
FEATURE [Part::Cylinder] Cylinder027
  Angle = 360
  AttacherType = Attacher::AttachEngine3D
  Height = 2
  Placement = pos=(19,-31.4,31) rot=(0,0,1;0rad)
  Radius = 2
FEATURE [Part::Chamfer] Chamfer009008024
  Base = -> Box025014013
  Edges = 1 edges r=4: [Edge8]
FEATURE [Part::Cut] Cut007002001007029003046  label="fan-duct-rev-2"
  Base = -> Cut007002001007029003042
  Tool = -> Cylinder025
FEATURE [Part::Feature] Cut007002001007029003046001  label="fan-duct-rev-2-refined"
  shape: bbox 52.67 x 64.46 x 26 mm, 198 faces (baked)
FEATURE [Part::Cut] Cut007002001007029003046002
  Base = -> Box025014014
  Tool = -> Cylinder026
FEATURE [Part::Chamfer] Chamfer009008025
  Base = -> Cut007002001007029003046002
  Edges = 1 edges r=1.5: [Edge9]
FEATURE [Part::Chamfer] Chamfer009008026
  Base = -> Chamfer009008025
  Edges = 1 edges r=2: [Edge15]
FEATURE [Part::Cut] Cut007002001007029003046003
  Base = -> Chamfer009008026
  Tool = -> Cylinder027
FEATURE [Part::MultiFuse] Fusion010020009006
  Shapes = -> [Chamfer009008024,Chamfer009008018,Cut007002001007029003046003]
FEATURE [Part::Chamfer] Chamfer009008027
  Base = -> Fusion010020009006
  Edges = 2 edges r=1: [Edge11,Edge19]
FEATURE [Part::Box] Box025014015  label="Cube057"
  AttacherType = Attacher::AttachEngine3D
  Height = 18.3
  Length = 1.7
  Placement = pos=(11.53,-33.9,9) rot=(0,0,1;0rad)
  Width = 5
FEATURE [Part::Feature] Fusion010020009002001  label="front-rev-1-refined"
  shape: bbox 43.24 x 28.92 x 64.47 mm, 118 faces (baked)
FEATURE [Part::Box] Box025014016  label="Cube058"
  AttacherType = Attacher::AttachEngine3D
  Height = 2.8
  Length = 5
  Placement = pos=(10,3,1.5) rot=(0,0,1;0rad)
  Width = 2
FEATURE [Part::Box] Box025014017  label="Cube059"
  AttacherType = Attacher::AttachEngine3D
  Height = 2.8
  Length = 5
  Placement = pos=(10,-8,1.5) rot=(0,0,1;0rad)
  Width = 2
FEATURE [Part::Box] Box025014018  label="Cube060"
  AttacherType = Attacher::AttachEngine3D
  Height = 2.8
  Length = 2
  Placement = pos=(3,-15,1.5) rot=(0,0,1;0rad)
  Width = 5
FEATURE [Part::Box] Box025014019  label="Cube061"
  AttacherType = Attacher::AttachEngine3D
  Height = 1
  Length = 2
  Placement = pos=(10,-10,1.5) rot=(0,0,1;0rad)
  Width = 17
FEATURE [Part::Box] Box025014020  label="Cube062"
  AttacherType = Attacher::AttachEngine3D
  Height = 1
  Length = 10
  Placement = pos=(1,-10,1.5) rot=(0,0,1;0rad)
  Width = 2
FEATURE [Part::MultiFuse] Fusion010020009007003  label="fan-support"
  Shapes = -> [Box025014016,Box025014019,Box025014017,Box025014020,Box025014018]
FEATURE [Part::MultiFuse] Fusion010020009007004  label="fan-w-support"
  Shapes = -> [Cut007002001007029003046001,Fusion010020009007003]
FEATURE [Part::MultiFuse] Fusion010020009007005
  Shapes = -> [Fusion010020009004,Fusion010020009005]
FEATURE [Part::Cut] Cut007002001007029003046004
  Base = -> Fusion010020009003
  Tool = -> Cylinder020
FEATURE [Part::Cut] Cut007002001007029003046005
  Base = -> Cut007002001007029003046004
  Tool = -> Fusion010020009007005
FEATURE [Part::Chamfer] Chamfer009008028
  Base = -> Cut007002001007029003046005
  Edges = 4 edges r=1: [Edge1,Edge8,Edge9,Edge10]
FEATURE [Part::Box] Box025014021  label="Cube063"
  AttacherType = Attacher::AttachEngine3D
  Height = 18.3
  Length = 1.7
  Placement = pos=(14.53,-33.9,9) rot=(0,0,1;0rad)
  Width = 5
FEATURE [Part::Box] Box025014022  label="Cube064"
  AttacherType = Attacher::AttachEngine3D
  Height = 18.3
  Length = 1.7
  Placement = pos=(17.53,-33.9,9) rot=(0,0,1;0rad)
  Width = 5
FEATURE [Part::Box] Box025014023  label="Cube065"
  AttacherType = Attacher::AttachEngine3D
  Height = 18.3
  Length = 2.7
  Placement = pos=(20.53,-33.9,9) rot=(0,0,1;0rad)
  Width = 5
FEATURE [Part::MultiFuse] Fusion010020009007006002  label="probe-custom-support"
  Shapes = -> [Box025014015,Box025014021,Box025014022,Box025014023]
FEATURE [Part::Cylinder] Cylinder028
  Angle = 360
  AttacherType = Attacher::AttachEngine3D
  Height = 19
  Placement = pos=(0,-33,0) rot=(0,0,1;0rad)
  Radius = 4.05
FEATURE [Part::Cut] Cut007002001007029003046006
  Base = -> Chamfer009008028
  Tool = -> Cylinder028
FEATURE [Part::Cut] Cut007002001007029003046007
  Base = -> Cut007002001007029003046006
  Tool = -> Box025014004
FEATURE [Part::Cut] Cut007002001007029003046008
  Base = -> Cut007002001007029003046007
  Tool = -> Box025014010
FEATURE [Part::Chamfer] Chamfer009008029
  Base = -> Cut007002001007029003046008
  Edges = 1 edges r=1: [Edge33]
FEATURE [Part::Chamfer] Chamfer009008030
  Base = -> Chamfer009008029
  Edges = 23 edges r=0.4: [Edge1,Edge2,Edge4,Edge7,Edge8,Edge9,Edge10,Edge11,Edge16,Edge20,Edge21,Edge23,Edge46,Edge47,Edge48,Edge53,Edge62,Edge64,Edge65,Edge66,Edge67,Edge87,Edge88]
FEATURE [Part::MultiFuse] Fusion010020009007006003  label="probe-mount-rev2"
  Shapes = -> [Chamfer009008030,Chamfer009008027]
FEATURE [Part::Feature] Fusion010020009007006003001  label="probe-mount-rev2-rf"
  shape: bbox 31.23 x 20 x 23.5 mm, 72 faces (baked)
FEATURE [Part::MultiFuse] Fusion010020009007006003002
  Shapes = -> [Fusion010020009007006003001,Fusion010020009007006002]
FEATURE [Part::Feature] Part__Feature012003  label="Body"
  shape: bbox 26.66 x 16.68 x 36.75 mm, 74 faces (baked)
FEATURE [Part::Feature] Part__Feature012004  label="Pin"
  shape: bbox 2.652 x 2.652 x 32.75 mm, 7 faces (baked)
FEATURE [App::Part] BLTouch_v3  label="BLTouch v3"
  Group = -> [Part__Feature012003,Part__Feature012004]
  Origin = -> Origin004
FEATURE [Part::MultiFuse] Fusion010020009007006003003  label="bl-touch"
  Placement = pos=(0,-34,36.75) rot=(0,0,1;0rad)
  Shapes = -> [Part__Feature012003,Part__Feature012004]
FEATURE [App::DocumentObjectGroup] Group  label="Preference"
  Group = -> [Part__Feature018,Part__Feature017,Part__Feature013,Part__Feature014,Part__Feature016,lower_4020_fan_duct,Cut007002001001,Cut007002001007,Cylinder005,Common,Part__Feature020,turbo_fan_35x18_2_,Cut007002001002005001,Cut007002001007029003046,Fusion010020009002,BLTouch_v3,Fusion010020009007006003003]
FEATURE [Part::Feature] Fusion010020009007006003004  label="probe-mount-rev003"
  shape: bbox 31.23 x 20 x 23.5 mm, 72 faces (baked)
FEATURE [Part::Box] Box025014024  label="Cube066"
  AttacherType = Attacher::AttachEngine3D
  Height = 11
  Length = 6
  Placement = pos=(7,-33.9,9) rot=(0,0,1;0rad)
  Width = 5
FEATURE [Part::Box] Box025014025  label="Cube067"
  AttacherType = Attacher::AttachEngine3D
  Height = 11
  Length = 26
  Placement = pos=(1,-33.9,27.5) rot=(0,0,1;0rad)
  Width = 5
FEATURE [Part::Box] Box025014026  label="Cube068"
  AttacherType = Attacher::AttachEngine3D
  Height = 7.5
  Length = 3.5
  Placement = pos=(7,-33.9,20) rot=(0,0,1;0rad)
  Width = 5
FEATURE [Part::Box] Box025014027  label="Cube069"
  AttacherType = Attacher::AttachEngine3D
  Height = 1
  Length = 4.5
  Placement = pos=(7,-33.9,26.5) rot=(0,0,1;0rad)
  Width = 5
FEATURE [Part::Feature] Cut007002001007029003046009  label="fan-duct-rev-2-refined001"
  shape: bbox 52.67 x 64.46 x 26 mm, 198 faces (baked)
FEATURE [Part::Cut] Cut007002001007029003046010
  Base = -> Fusion010020009007006003004
  Tool = -> Box025014025
FEATURE [Part::MultiFuse] Fusion010020009007006003005
  Shapes = -> [Box025014024,Box025014027,Cut007002001007029003046010,Box025014026,Cut007002001007029003046009]
FEATURE [Part::Box] Box025014028  label="Cube070"
  AttacherType = Attacher::AttachEngine3D
  Height = 10
  Length = 10
  Placement = pos=(-3.77,-35.5,26.5) rot=(0,0,1;0rad)
  Width = 10
FEATURE [Part::Chamfer] Chamfer009008031
  Base = -> Box025014028
  Edges = 1 edges r=1: [Edge8]
FEATURE [Part::Cut] Cut007002001007029003046011
  Base = -> Fusion010020009007006003005
  Tool = -> Chamfer009008031
FEATURE [Part::Cylinder] Cylinder029
  Angle = 360
  AttacherType = Attacher::AttachEngine3D
  Height = 6.5
  Placement = pos=(19,-31.4,21) rot=(0,0,1;0rad)
  Radius = 1
FEATURE [Part::Feature] Fusion010020009007003001  label="fan-support001"
  shape: bbox 14 x 22 x 2.8 mm, 26 faces (baked)
FEATURE [Part::Box] Box025014029  label="Cube071"
  AttacherType = Attacher::AttachEngine3D
  Height = 5.2
  Length = 5.2
  Placement = pos=(7.9,-33.9,1.5) rot=(0,0,1;0rad)
  Width = 5
FEATURE [Part::Chamfer] Chamfer009008032
  Base = -> Box025014029
  Edges = 1 edges r=5.1: [Edge4]
  Placement = pos=(0,0,2.3) rot=(0,0,1;0rad)
FEATURE [Part::MultiFuse] Fusion010020009007006003006  label="duct-probe-combined-rev-2"
  Shapes = -> [Cylinder029,Cut007002001007029003046011,Chamfer009008032]
FEATURE [Part::Feature] Fusion010020009007006003006001  label="duct-probe-combined-rev-003"
  shape: bbox 59.23 x 64.46 x 26 mm, 260 faces (baked)
FEATURE [Part::MultiFuse] Fusion010020009007006003006002  label="duct-probe-combined-rev-2-w-support"
  Shapes = -> [Fusion010020009007006003006001,Fusion010020009007003001]
FEATURE [Part::Feature] Cut007002001007029003046001001  label="fan-duct-rev-2-refined002"
  shape: bbox 52.67 x 64.46 x 26 mm, 198 faces (baked)
FEATURE [Part::Box] Box025014031  label="Cube072"
  AttacherType = Attacher::AttachEngine3D
  Height = 3
  Length = 12
  Placement = pos=(-6,-13,0) rot=(0,0,1;0rad)
  Width = 26
FEATURE [Part::Cylinder] Cylinder030
  Angle = 360
  AttacherType = Attacher::AttachEngine3D
  Height = 10
  Radius = 2
FEATURE [Part::Cylinder] Cylinder031
  Angle = 360
  AttacherType = Attacher::AttachEngine3D
  Height = 10
  Placement = pos=(0,9,0) rot=(0,0,1;0rad)
  Radius = 1.6
FEATURE [Part::Cylinder] Cylinder032
  Angle = 360
  AttacherType = Attacher::AttachEngine3D
  Height = 10
  Placement = pos=(0,-9,0) rot=(0,0,1;0rad)
  Radius = 1.6
FEATURE [Part::MultiFuse] Fusion010020009007006003006003
  Shapes = -> [Cylinder031,Cylinder030,Cylinder032]
FEATURE [Part::Cut] Cut007002001007029003046001002
  Base = -> Box025014031
  Placement = pos=(0,-44.9,45) rot=(0,0,1;0rad)
  Tool = -> Fusion010020009007006003006003
FEATURE [Part::Feature] Part__Feature012005001  label="Body002"
  shape: bbox 26.66 x 16.68 x 36.75 mm, 74 faces (baked)
FEATURE [Part::Feature] Part__Feature012006001  label="Pin002"
  shape: bbox 2.652 x 2.652 x 32.75 mm, 7 faces (baked)
FEATURE [Part::MultiFuse] Fusion010020009007006003006004  label="bltouch"
  Placement = pos=(1.08579,-43.7796,0) rot=(0,0,-1;4.36332rad)
  Shapes = -> [Part__Feature012005001,Part__Feature012006001]
FEATURE [Part::Feature] Fusion010020009007006003006004001  label="bltouch001"
  Placement = pos=(-1,-3,45.7) rot=(0,0,1;0rad)
  shape: bbox 17.53 x 25.05 x 42.75 mm, 81 faces, 2 solids (baked)
FEATURE [Part::Box] Box025014032  label="Cube073"
  AttacherType = Attacher::AttachEngine3D
  Height = 35
  Length = 17.5
  Placement = pos=(-7,-33.9,16.5) rot=(0,0,1;0rad)
  Width = 5
FEATURE [Part::Box] Box025014033  label="Cube074"
  AttacherType = Attacher::AttachEngine3D
  Height = 5
  Length = 17.5
  Placement = pos=(-7,-59.9,46) rot=(0,0,1;0rad)
  Width = 26
FEATURE [Part::Feature] Fusion010020009007006003006004002001  label="Fusion010020009007006003006004003"
  Placement = pos=(-0.25,0,4) rot=(0,0,1;0rad)
  shape: bbox 9.356 x 20.11 x 10 mm, 9 faces, 3 solids (baked)
FEATURE [Part::Box] Box025014034  label="Cube075"
  AttacherType = Attacher::AttachEngine3D
  Height = 24.25
  Length = 24.25
  Placement = pos=(10.5,-33.9,26.75) rot=(0,0,1;0rad)
  Width = 5
FEATURE [Part::Chamfer] Chamfer009008033
  Base = -> Box025014034
  Edges = 2 edges r=20: [Edge4,Edge6]
  Placement = pos=(-4.25,0,0) rot=(0,0,1;0rad)
FEATURE [Part::Box] Box025014035  label="Cube076"
  AttacherType = Attacher::AttachEngine3D
  Height = 5
  Length = 5
  Placement = pos=(10.25,-33.9,26.75) rot=(0,0,1;0rad)
  Width = 5
FEATURE [Part::Box] Box025014036  label="Cube077"
  AttacherType = Attacher::AttachEngine3D
  Height = 7
  Length = 9.5
  Placement = pos=(26,-33.9,25) rot=(0,0,1;0rad)
  Width = 5
FEATURE [Part::Chamfer] Chamfer009008034
  Base = -> Box025014036
  Edges = 1 edges r=6: [Edge6]
FEATURE [Part::MultiFuse] Fusion010020009007006003006004002002
  Placement = pos=(0,0,-1.75) rot=(0,0,1;0rad)
  Shapes = -> [Chamfer009008033,Chamfer009008034]
FEATURE [Part::Chamfer] Chamfer009008035
  Base = -> Box025014035
  Edges = 1 edges r=4.25: [Edge6]
  Placement = pos=(-0.5,0,0) rot=(0,0,1;0rad)
FEATURE [Part::Chamfer] Chamfer009008036
  Base = -> Box025014033
  Edges = 1 edges: [Edge1 r1=11 r2=8]
FEATURE [Part::Chamfer] Chamfer009008037
  Base = -> Chamfer009008036
  Edges = 1 edges r=5: [Edge15]
FEATURE [Part::Box] Box025014037  label="Cube078"
  AttacherType = Attacher::AttachEngine3D
  Height = 10
  Length = 9
  Placement = pos=(5.5,-38.9,43) rot=(0,0,1;0rad)
  Width = 5
FEATURE [Part::Cut] Cut007002001007029003046001003
  Base = -> Chamfer009008037
  Tool = -> Fusion010020009007006003006004002001
FEATURE [Part::Cut] Cut007002001007029003046001004
  Base = -> Cut007002001007029003046001003
  Tool = -> Box025014037
FEATURE [Part::Chamfer] Chamfer009008038
  Base = -> Box025014032
  Edges = 1 edges r=17.23: [Edge4]
FEATURE [Part::Chamfer] Chamfer009008039
  Base = -> Cut007002001007029003046001004
  Edges = 1 edges r=1: [Edge24]
FEATURE [Part::Chamfer] Chamfer009008040
  Base = -> Chamfer009008039
  Edges = 1 edges r=3: [Edge26]
  Placement = pos=(0,0,-1.75) rot=(0,0,1;0rad)
FEATURE [Part::Box] Box025014039  label="Cube080"
  AttacherType = Attacher::AttachEngine3D
  Height = 10
  Length = 10
  Placement = pos=(-4,-53.5,-5.3) rot=(0,0,1;0rad)
  Width = 10
FEATURE [Part::Cut] Cut007002001007029003046001005  label="bltouch-pos"
  Base = -> Fusion010020009007006003006004001
  Placement = pos=(0,0,-1.75) rot=(0,0,1;0rad)
  Tool = -> Box025014039
FEATURE [Part::Box] Box025014040  label="Cube081"
  AttacherType = Attacher::AttachEngine3D
  Height = 10
  Length = 22
  Placement = pos=(-10,-37,49.25) rot=(0,0,1;0rad)
  Width = 10
FEATURE [Part::Cut] Cut007002001007029003046001006
  Base = -> Chamfer009008038
  Tool = -> Box025014040
FEATURE [Part::MultiFuse] Fusion010020009007006003006004002003  label="duct-with-bltouch-rev1"
  Shapes = -> [Cut007002001007029003046001001,Cut007002001007029003046001006,Chamfer009008040,Fusion010020009007006003006004002002,Chamfer009008035]
